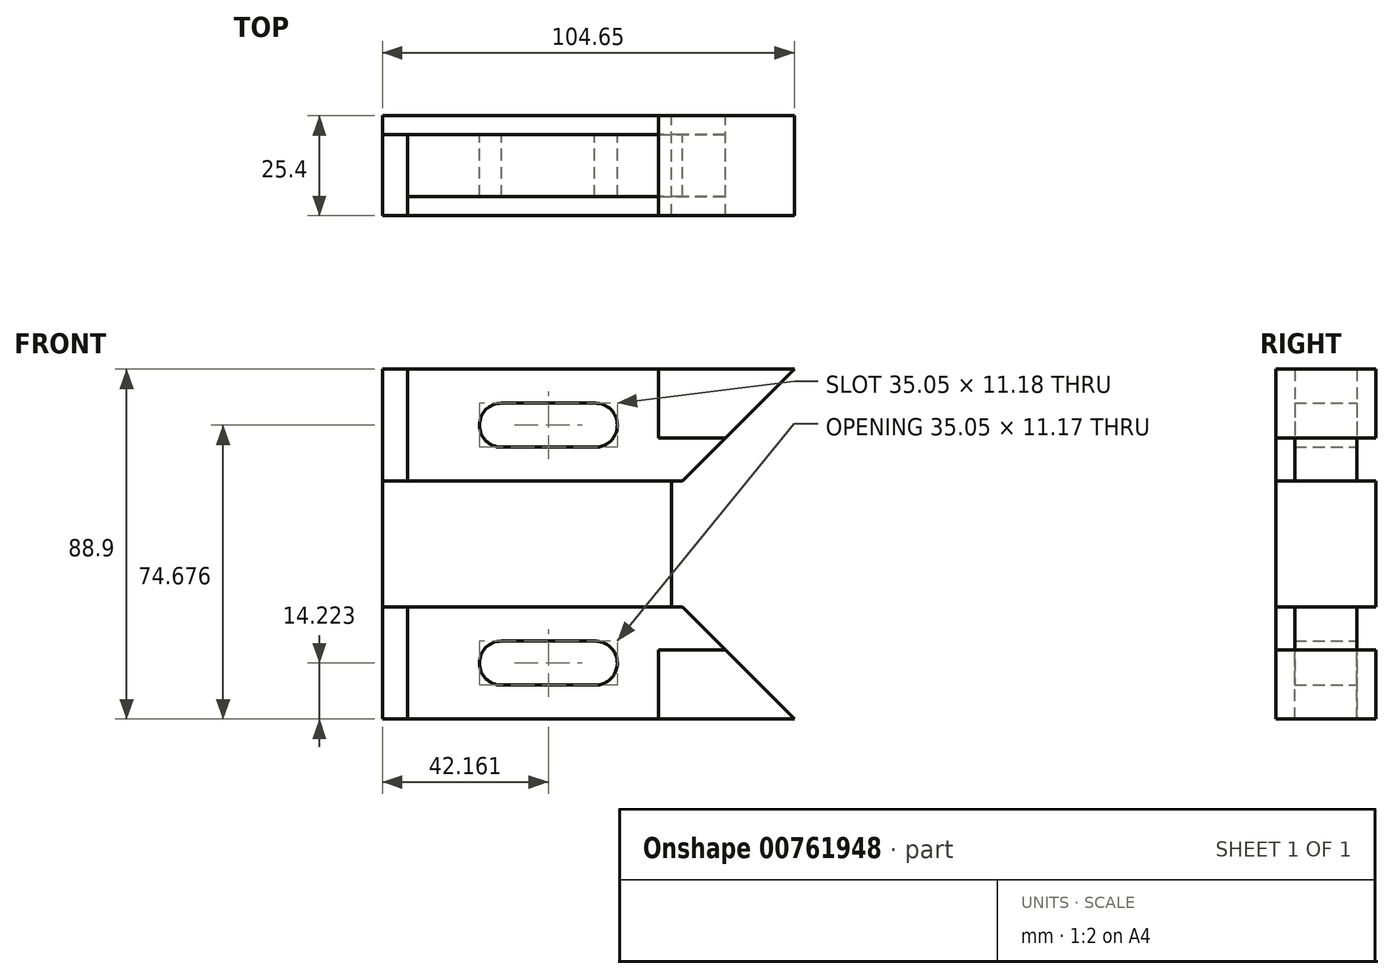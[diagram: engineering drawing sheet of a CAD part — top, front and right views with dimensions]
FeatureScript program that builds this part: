
annotation { "Feature Type Name" : "Feature", "Feature Type Description" : "" }
export const myFeature = defineFeature(function(context is Context, id is Id, definition is map)
    precondition{}
    {
        {
            var Q0;
            Q0=qCreatedBy(makeId("Front.planeOp"),FACE);
            var sketch = newSketch(context, id + "F0", { "sketchPlane" : qUnion([Q0])});
            skLineSegment(sketch, "E0.bottom", {"start": v(36.7, 16) * mm, "end": v(-36.7, 16) * mm});
            skLineSegment(sketch, "E0.top", {"start": v(36.7, -16) * mm, "end": v(-36.7, -16) * mm});
            skLineSegment(sketch, "E0.left", {"start": v(36.7, 16) * mm, "end": v(36.7, -16) * mm});
            skLineSegment(sketch, "E0.right", {"start": v(-36.7, 16) * mm, "end": v(-36.7, -16) * mm});
            skPoint(sketch, "E0.middle", {"position": v(0, 0) * mm});
            skLineSegment(sketch, "E1", {"start": v(-36.7, 16) * mm, "end": v(-36.7, 44.45) * mm});
            skLineSegment(sketch, "E2", {"start": v(-36.7, -16) * mm, "end": v(-36.7, -44.45) * mm});
            skLineSegment(sketch, "E3", {"start": v(-36.7, -44.45) * mm, "end": v(67.95, -44.45) * mm});
            skLineSegment(sketch, "E4", {"start": v(-36.7, 44.45) * mm, "end": v(67.95, 44.45) * mm});
            skLineSegment(sketch, "E5", {"start": v(39.5, 16) * mm, "end": v(36.7, 16) * mm});
            skLineSegment(sketch, "E6", {"start": v(36.7, -16) * mm, "end": v(39.5, -16) * mm});
            skLineSegment(sketch, "E7", {"start": v(67.95, 44.45) * mm, "end": v(39.5, 16) * mm});
            skLineSegment(sketch, "E8", {"start": v(67.95, -44.45) * mm, "end": v(39.5, -16) * mm});
            skPoint(sketch, "E9.orphan", {"position": v(67.95, -16) * mm});
            skPoint(sketch, "E10.end.orphan", {"position": v(68.54, 16) * mm});
            skPoint(sketch, "E11.startSnap0", {"position": v(-36.7, 30.23) * mm});
            skLineSegment(sketch, "E12", {"start": v(-30.35, 44.45) * mm, "end": v(-30.35, 16) * mm});
            skLineSegment(sketch, "E13", {"start": v(-30.35, -44.45) * mm, "end": v(-30.35, -16) * mm});
            skPoint(sketch, "E14.end.orphan", {"position": v(-30.35, -38.7) * mm});
            skPoint(sketch, "E14.start.orphan", {"position": v(-36.7, -38.7) * mm});
            skPoint(sketch, "E11.end.orphan", {"position": v(-36.7, 30.23) * mm});
            skPoint(sketch, "E11.start.orphan", {"position": v(-30.35, 30.23) * mm});
            skLineSegment(sketch, "E15", {"start": v(33.5, -44.45) * mm, "end": v(33.5, -26.92) * mm});
            skLineSegment(sketch, "E16", {"start": v(33.5, 44.45) * mm, "end": v(33.5, 26.92) * mm});
            skLineSegment(sketch, "E17", {"start": v(33.5, 26.92) * mm, "end": v(50.42, 26.92) * mm});
            skLineSegment(sketch, "E18", {"start": v(33.5, -26.92) * mm, "end": v(50.42, -26.92) * mm});
            skPoint(sketch, "E19.end.orphan", {"position": v(33.5, -52.36) * mm});
            skPoint(sketch, "E20.start.orphan", {"position": v(-30.35, -30.23) * mm});
            skLineSegment(sketch, "E21", {"start": v(-6.48, -35.81) * mm, "end": v(17.4, -35.81) * mm});
            skLineSegment(sketch, "E22", {"start": v(-6.48, 35.81) * mm, "end": v(17.4, 35.81) * mm});
            skLineSegment(sketch, "E23", {"start": v(-6.48, 24.64) * mm, "end": v(17.4, 24.64) * mm});
            skArc(sketch, "E24", {"start": v(-6.48, -24.64) * mm, "mid": v(-12.06, -30.23) * mm, "end": v(-6.48, -35.81) * mm});
            skArc(sketch, "E25", {"start": v(17.4, -35.81) * mm, "mid": v(22.99, -30.15) * mm, "end": v(17.24, -24.64) * mm});
            skLineSegment(sketch, "E26", {"start": v(-6.48, -24.64) * mm, "end": v(17.56, -24.64) * mm});
            skLineSegment(sketch, "E27", {"start": v(17.4, -35.81) * mm, "end": v(-6.48, -35.81) * mm});
            skPoint(sketch, "E28.orphan", {"position": v(22.99, -24.64) * mm});
            skPoint(sketch, "E29.start.orphan", {"position": v(22.99, -35.81) * mm});
            skPoint(sketch, "E30.orphan", {"position": v(22.99, -30.23) * mm});
            skPoint(sketch, "E31.start.orphan", {"position": v(11.81, -30.23) * mm});
            skLineSegment(sketch, "E32.trimOffspring", {"start": v(-6.48, -35.81) * mm, "end": v(-6.48, -35.81) * mm});
            skArc(sketch, "E33", {"start": v(-6.48, 35.81) * mm, "mid": v(-12.06, 30.23) * mm, "end": v(-6.48, 24.64) * mm});
            skArc(sketch, "E34", {"start": v(17.4, 24.64) * mm, "mid": v(22.99, 30.23) * mm, "end": v(17.4, 35.81) * mm});
            skLineSegment(sketch, "E35", {"start": v(17.4, 35.81) * mm, "end": v(-6.48, 35.81) * mm});
            skPoint(sketch, "E36.orphan", {"position": v(22.99, 35.81) * mm});
            skPoint(sketch, "E37.orphan", {"position": v(22.99, 24.64) * mm});
            skPoint(sketch, "E38.trimOffspring.end.orphan", {"position": v(22.99, 30.23) * mm});
            skSolve(sketch);
        }
        {
            var Q0;
            {var subQ3=sQuery(id+"F0.wireOp",EDGE,"E16");Q0=makeQuery(id+"F0.imprint","IMPRINT",FACE,{"disambiguationData":[TD([[makeQuery(id+"F0.imprint","IMPRINT",EDGE,{"derivedFrom":subQ3}),1.0]])]});}
            var Q1;
            {var subQ3=sQuery(id+"F0.wireOp",EDGE,"E0.left");Q1=makeQuery(id+"F0.imprint","IMPRINT",FACE,{"disambiguationData":[TD([[makeQuery(id+"F0.imprint","IMPRINT",EDGE,{"derivedFrom":subQ3}),-1.0]])]});}
            var Q2;
            {var subQ3=sQuery(id+"F0.wireOp",EDGE,"E15");Q2=makeQuery(id+"F0.imprint","IMPRINT",FACE,{"disambiguationData":[TD([[makeQuery(id+"F0.imprint","IMPRINT",EDGE,{"derivedFrom":subQ3}),-1.0]])]});}
            extrude(context, id + "F1", {"entities" : qUnion([Q0, Q1, Q2]), "depth" : 25.4 * mm, "offsetDistance" : 25.4 * mm, "symmetric" : true});
        }
        {
            var Q0;
            {var subQ4=sQuery(id+"F0.wireOp",EDGE,"E5");Q0=makeQuery(id+"F0.imprint","IMPRINT",FACE,{"disambiguationData":[TD([[makeQuery(id+"F0.imprint","IMPRINT",EDGE,{"derivedFrom":subQ4}),-1.0]])]});}
            var Q1;
            {var subQ6=sQuery(id+"F0.wireOp",EDGE,"E6");Q1=makeQuery(id+"F0.imprint","IMPRINT",FACE,{"disambiguationData":[TD([[makeQuery(id+"F0.imprint","IMPRINT",EDGE,{"derivedFrom":subQ6}),-1.0]])]});}
            extrude(context, id + "F2", {"entities" : qUnion([Q0, Q1]), "depth" : 15.75 * mm, "offsetDistance" : 25.4 * mm, "symmetric" : true});
        }
        {
            var Q0;
            {var subQ0=sQuery(id+"F0.wireOp",EDGE,"E1");Q0=makeQuery(id+"F0.imprint","IMPRINT",FACE,{"disambiguationData":[TD([[makeQuery(id+"F0.imprint","IMPRINT",EDGE,{"derivedFrom":subQ0}),-1.0]])]});}
            extrude(context, id + "F3", {"entities" : qUnion([Q0]), "depth" : 12.7 * mm, "offsetDistance" : 25.4 * mm, "hasSecondDirection" : true, "secondDirectionOppositeDirection" : true, "secondDirectionDepth" : 7.87 * mm});
        }
        {
            var Q0;
            {var subQ0=sQuery(id+"F0.wireOp",EDGE,"E2");Q0=makeQuery(id+"F0.imprint","IMPRINT",FACE,{"disambiguationData":[TD([[makeQuery(id+"F0.imprint","IMPRINT",EDGE,{"derivedFrom":subQ0}),1.0]])]});}
            extrude(context, id + "F4", {"entities" : qUnion([Q0]), "depth" : 12.7 * mm, "offsetDistance" : 25.4 * mm, "hasSecondDirection" : true, "secondDirectionOppositeDirection" : true, "secondDirectionDepth" : 7.87 * mm});
        }
    });
